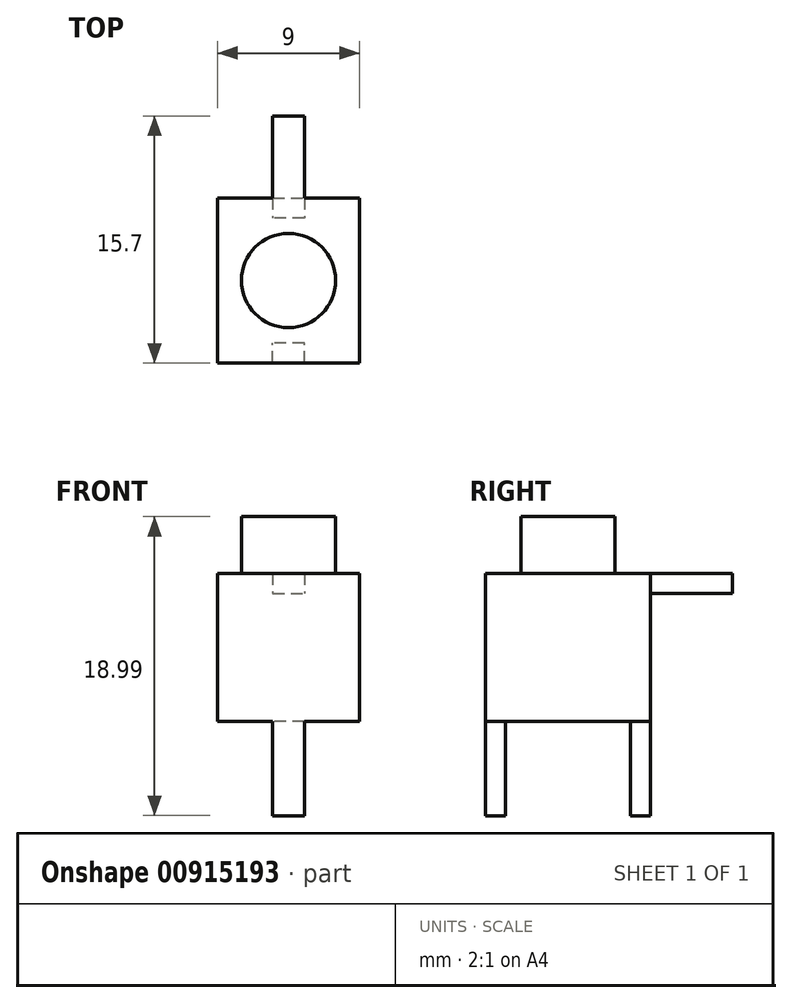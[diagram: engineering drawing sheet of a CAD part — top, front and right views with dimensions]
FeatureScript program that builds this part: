
annotation { "Feature Type Name" : "Feature", "Feature Type Description" : "" }
export const myFeature = defineFeature(function(context is Context, id is Id, definition is map)
    precondition{}
    {
        {
            var Q0;
            Q0=qCreatedBy(makeId("Top.planeOp"),FACE);
            var sketch = newSketch(context, id + "F0", { "sketchPlane" : qUnion([Q0])});
            skLineSegment(sketch, "E0.bottom", {"start": v(4.5, 5.25) * mm, "end": v(-4.5, 5.25) * mm});
            skLineSegment(sketch, "E0.top", {"start": v(4.5, -5.25) * mm, "end": v(-4.5, -5.25) * mm});
            skLineSegment(sketch, "E0.left", {"start": v(4.5, 5.25) * mm, "end": v(4.5, -5.25) * mm});
            skLineSegment(sketch, "E0.right", {"start": v(-4.5, 5.25) * mm, "end": v(-4.5, -5.25) * mm});
            skPoint(sketch, "E0.middle", {"position": v(0, 0) * mm});
            skSolve(sketch);
        }
        {
            var Q0;
            Q0=makeQuery(id+"F0.imprint","IMPRINT",FACE,{"disambiguationData":[TD([[makeQuery(id+"F0.imprint","IMPRINT",EDGE,{"derivedFrom":sQuery(id+"F0.wireOp",EDGE,"E0.bottom")}),1.0]])]});
            extrude(context, id + "F1", {"entities" : qUnion([Q0]), "depth" : 9.4 * mm, "offsetDistance" : 25.4 * mm});
        }
        {
            var Q0;
            Q0=makeQuery(id+"F1.opExtrude","CAP_FACE",FACE,{"disambiguationData":[OSD([sQuery(id+"F0.wireOp",EDGE,"E0.bottom"),sQuery(id+"F0.wireOp",EDGE,"E0.top"),sQuery(id+"F0.wireOp",EDGE,"E0.left"),sQuery(id+"F0.wireOp",EDGE,"E0.right")])],"isStart":false});
            var sketch = newSketch(context, id + "F2", { "sketchPlane" : qUnion([Q0])});
            skCircle(sketch, "E1", {"center": v(0, 0) * mm, "radius": 3 * mm});
            skSolve(sketch);
        }
        {
            var Q0;
            Q0=makeQuery(id+"F2.imprint","IMPRINT",FACE,{"disambiguationData":[TD([[makeQuery(id+"F2.imprint","IMPRINT",EDGE,{"derivedFrom":sQuery(id+"F2.wireOp",EDGE,"E1")}),1.0]])]});
            extrude(context, id + "F3", {"entities" : qUnion([Q0]), "operationType" : NewBodyOperationType.ADD, "depth" : 3.6 * mm, "offsetDistance" : 25.4 * mm});
        }
        {
            var Q0;
            Q0=makeQuery(id+"F1.opExtrude","SWEPT_FACE",FACE,{"disambiguationData":[OSD([sQuery(id+"F0.wireOp",EDGE,"E0.bottom")])]});
            var sketch = newSketch(context, id + "F4", { "sketchPlane" : qUnion([Q0])});
            skLineSegment(sketch, "E2.bottom", {"start": v(1, 9.4) * mm, "end": v(-1, 9.4) * mm});
            skLineSegment(sketch, "E2.top", {"start": v(1, 8.13) * mm, "end": v(-1, 8.13) * mm});
            skLineSegment(sketch, "E2.left", {"start": v(1, 9.4) * mm, "end": v(1, 8.13) * mm});
            skLineSegment(sketch, "E2.right", {"start": v(-1, 9.4) * mm, "end": v(-1, 8.13) * mm});
            skSolve(sketch);
        }
        {
            var Q0;
            Q0=makeQuery(id+"F4.imprint","IMPRINT",FACE,{"disambiguationData":[TD([[makeQuery(id+"F4.imprint","IMPRINT",EDGE,{"derivedFrom":sQuery(id+"F4.wireOp",EDGE,"E2.bottom")}),-1.0]])]});
            extrude(context, id + "F5", {"entities" : qUnion([Q0]), "operationType" : NewBodyOperationType.ADD, "depth" : 5.2 * mm, "offsetDistance" : 25.4 * mm});
        }
        {
            var Q0;
            Q0=makeQuery(id+"F1.opExtrude","CAP_FACE",FACE,{"disambiguationData":[OSD([sQuery(id+"F0.wireOp",EDGE,"E0.bottom"),sQuery(id+"F0.wireOp",EDGE,"E0.top"),sQuery(id+"F0.wireOp",EDGE,"E0.left"),sQuery(id+"F0.wireOp",EDGE,"E0.right")])],"isStart":true});
            var sketch = newSketch(context, id + "F6", { "sketchPlane" : qUnion([Q0])});
            skLineSegment(sketch, "E3.bottom", {"start": v(1, -5.25) * mm, "end": v(-1, -5.25) * mm});
            skLineSegment(sketch, "E3.top", {"start": v(1, -3.98) * mm, "end": v(-1, -3.98) * mm});
            skLineSegment(sketch, "E3.left", {"start": v(1, -5.25) * mm, "end": v(1, -3.98) * mm});
            skLineSegment(sketch, "E3.right", {"start": v(-1, -5.25) * mm, "end": v(-1, -3.98) * mm});
            skLineSegment(sketch, "E4.bottom", {"start": v(1, 5.25) * mm, "end": v(-1, 5.25) * mm});
            skLineSegment(sketch, "E4.top", {"start": v(1, 3.98) * mm, "end": v(-1, 3.98) * mm});
            skLineSegment(sketch, "E4.left", {"start": v(1, 5.25) * mm, "end": v(1, 3.98) * mm});
            skLineSegment(sketch, "E4.right", {"start": v(-1, 5.25) * mm, "end": v(-1, 3.98) * mm});
            skSolve(sketch);
        }
        {
            var Q0;
            Q0=makeQuery(id+"F6.imprint","IMPRINT",FACE,{"disambiguationData":[TD([[makeQuery(id+"F6.imprint","IMPRINT",EDGE,{"derivedFrom":sQuery(id+"F6.wireOp",EDGE,"E4.bottom")}),1.0]])]});
            var Q1;
            Q1=makeQuery(id+"F6.imprint","IMPRINT",FACE,{"disambiguationData":[TD([[makeQuery(id+"F6.imprint","IMPRINT",EDGE,{"derivedFrom":sQuery(id+"F6.wireOp",EDGE,"E3.bottom")}),-1.0]])]});
            extrude(context, id + "F7", {"entities" : qUnion([Q0, Q1]), "operationType" : NewBodyOperationType.ADD, "depth" : 6 * mm, "offsetDistance" : 25.4 * mm});
        }
    });
